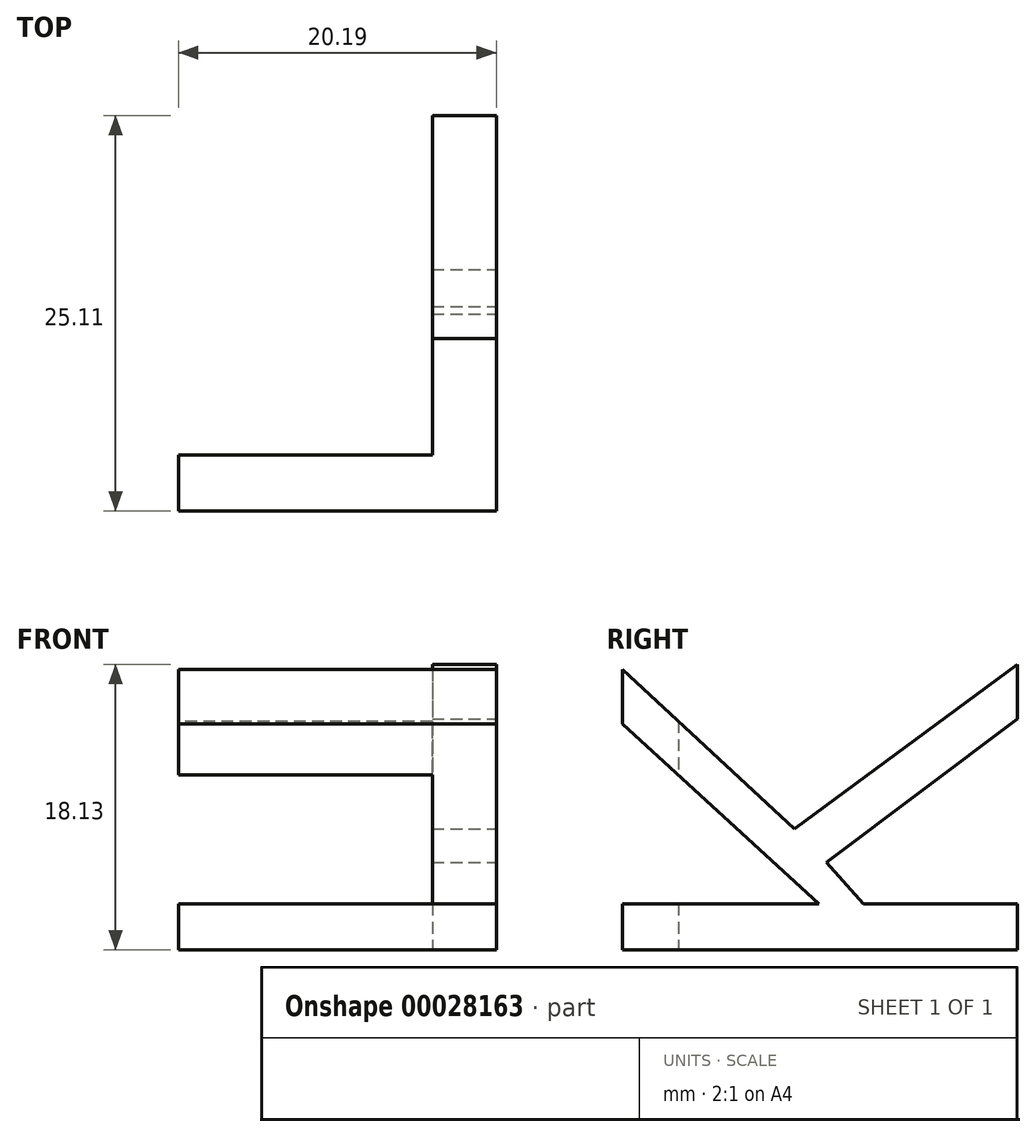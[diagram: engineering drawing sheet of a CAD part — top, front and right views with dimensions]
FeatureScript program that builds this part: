
annotation { "Feature Type Name" : "Feature", "Feature Type Description" : "" }
export const myFeature = defineFeature(function(context is Context, id is Id, definition is map)
    precondition{}
    {
        {
            var Q0;
            Q0=qCreatedBy(makeId("Top.planeOp"),FACE);
            var sketch = newSketch(context, id + "F0", { "sketchPlane" : qUnion([Q0])});
            skLineSegment(sketch, "E0.bottom", {"start": v(-16.99, 8.8) * mm, "end": v(8.41, 8.8) * mm});
            skLineSegment(sketch, "E0.top", {"start": v(-16.99, -16.6) * mm, "end": v(8.41, -16.6) * mm});
            skLineSegment(sketch, "E0.left", {"start": v(-16.99, 8.8) * mm, "end": v(-16.99, -16.6) * mm});
            skLineSegment(sketch, "E0.right", {"start": v(8.41, 8.8) * mm, "end": v(8.41, -16.6) * mm});
            skSolve(sketch);
        }
        {
            var Q0;
            Q0=makeQuery(id+"F0.imprint","IMPRINT",FACE,{"disambiguationData":[TD([[makeQuery(id+"F0.imprint","IMPRINT",EDGE,{"derivedFrom":sQuery(id+"F0.wireOp",EDGE,"E0.bottom")}),-1.0]])]});
            extrude(context, id + "F1", {"entities" : qUnion([Q0]), "endBound" : BoundingType.SYMMETRIC, "depth" : 25.4 * mm});
        }
        {
            var Q0;
            Q0=makeQuery(id+"F1.opExtrude","SWEPT_FACE",FACE,{"disambiguationData":[OSD([sQuery(id+"F0.wireOp",EDGE,"E0.right")])]});
            var sketch = newSketch(context, id + "F2", { "sketchPlane" : qUnion([Q0])});
            skText(sketch, "E1", { "text": "K", "fontName": "OpenSans-Regular.ttf"});
            const initialGuessF2  = {"E1": [0.00888, -0.016, 0, 1, 0.0254]};
            skSetInitialGuess(sketch, initialGuessF2);
            skSolve(sketch);
        }
        {
            var Q0;
            Q0=makeQuery(id+"F1.opExtrude","CAP_FACE",FACE,{"disambiguationData":[OSD([sQuery(id+"F0.wireOp",EDGE,"E0.bottom"),sQuery(id+"F0.wireOp",EDGE,"E0.top"),sQuery(id+"F0.wireOp",EDGE,"E0.left"),sQuery(id+"F0.wireOp",EDGE,"E0.right")])],"isStart":true});
            var sketch = newSketch(context, id + "F3", { "sketchPlane" : qUnion([Q0])});
            skText(sketch, "E2", { "text": "L", "fontName": "OpenSans-Regular.ttf"});
            const initialGuessF3  = {"E2": [0.01362, 0.0166, -1, 0, 0.03686]};
            skSetInitialGuess(sketch, initialGuessF3);
            skSolve(sketch);
        }
        {
            var Q0;
            {var subQ5=sQuery(id+"F2.wireOp",EDGE,"E1.sketch_text.stroke-2");Q0=makeQuery(id+"F2.imprint","IMPRINT",FACE,{"disambiguationData":[TD([[makeQuery(id+"F2.imprint","IMPRINT",EDGE,{"derivedFrom":subQ5}),1.0]])]});}
            var Q1;
            {var subQ9=sQuery(id+"F2.wireOp",EDGE,"E1.sketch_text.stroke-6");Q1=makeQuery(id+"F2.imprint","IMPRINT",FACE,{"disambiguationData":[TD([[makeQuery(id+"F2.imprint","IMPRINT",EDGE,{"derivedFrom":subQ9}),1.0]])]});}
            extrude(context, id + "F4", {"entities" : qUnion([Q0, Q1]), "operationType" : NewBodyOperationType.REMOVE, "oppositeDirection" : true, "depth" : 38.1 * mm});
        }
        {
            var Q0;
            {var subQ6=sQuery(id+"F3.wireOp",EDGE,"E2.sketch_text.stroke-3");Q0=makeQuery(id+"F3.imprint","IMPRINT",FACE,{"disambiguationData":[TD([[makeQuery(id+"F3.imprint","IMPRINT",EDGE,{"derivedFrom":subQ6}),1.0]])]});}
            extrude(context, id + "F5", {"entities" : qUnion([Q0]), "operationType" : NewBodyOperationType.REMOVE, "oppositeDirection" : true, "depth" : 35.56 * mm});
        }
    });
